AUTODESK INVENTOR PART (.ipt)
format: ipt  version: 2012 (Build 160160000, 160)  size: 70,144 bytes
history: native  units: in
note: dims shown in document units (in); Inventor stores cm internally (conversion verified against a paired STEP export)
features: sketch x1
ambient origin geometry x8: Origin, YZ Plane, XZ Plane, XY Plane, X Axis, Y Axis, Z Axis, Center Point
feature tree (1):
  sketch  "Sketch1"  dims[d0=28.0in d1=9.636in d5=0.938in d6=8.5in d7=2.5in d8=19.5in d9=8.074in d10=21.5in d11=7.5in d14=6.2833in d17=4.0in d18=6.25in d19=25.0in d20=7.4204in d21=1.25in]
